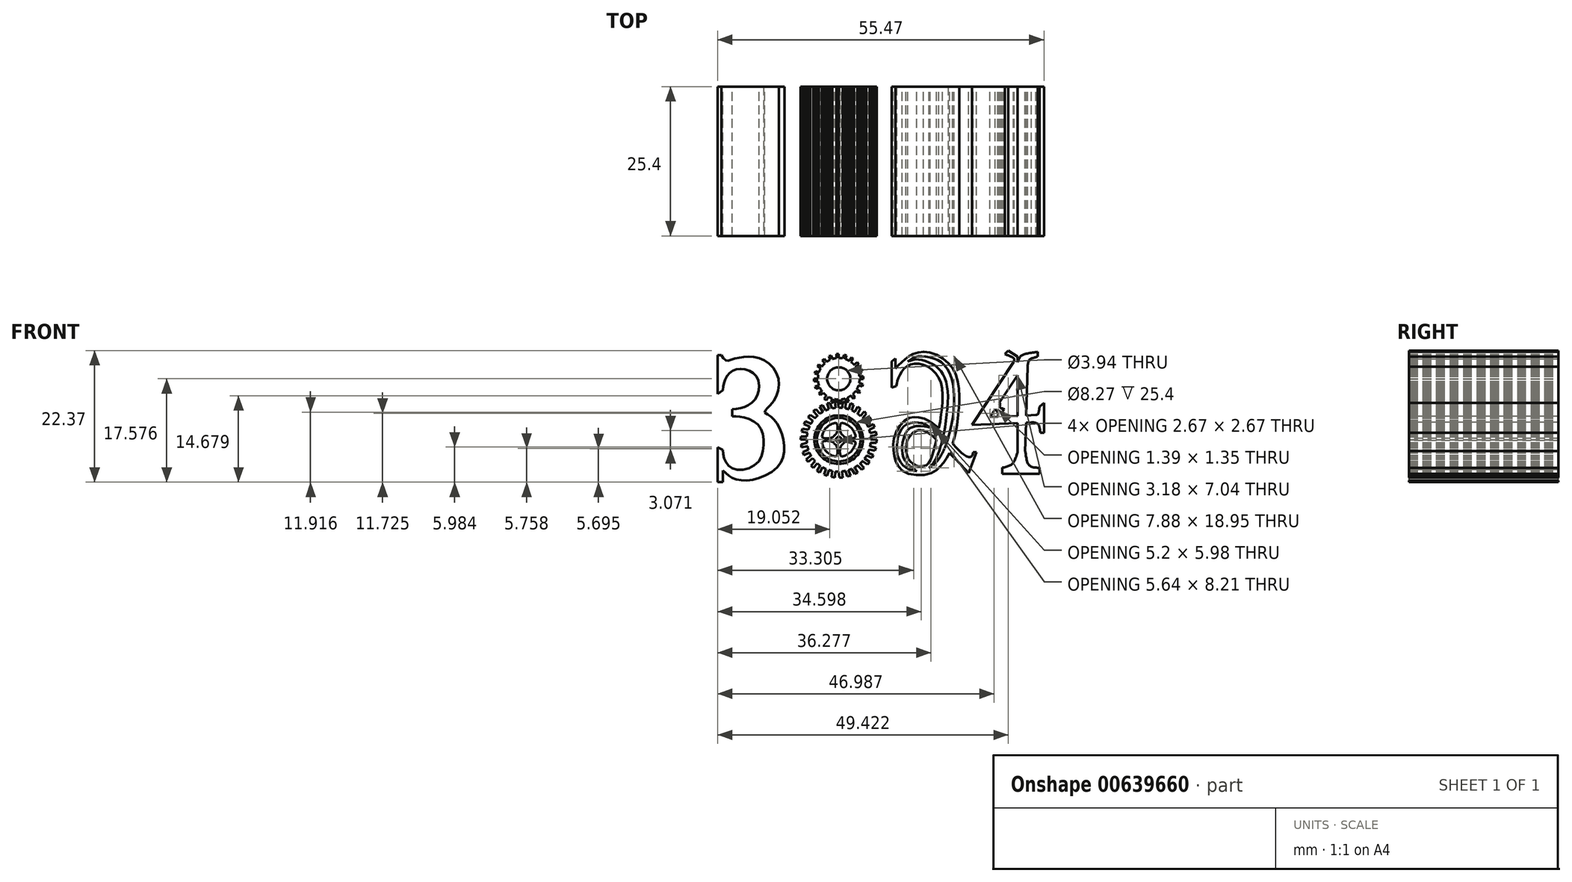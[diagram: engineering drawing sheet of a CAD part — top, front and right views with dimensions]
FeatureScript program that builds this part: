
annotation { "Feature Type Name" : "Feature", "Feature Type Description" : "" }
export const myFeature = defineFeature(function(context is Context, id is Id, definition is map)
    precondition{}
    {
        {
            var Q0;
            Q0=qCreatedBy(makeId("Front.planeOp"),FACE);
            var sketch = newSketch(context, id + "F0", { "sketchPlane" : qUnion([Q0])});
            skLineSegment(sketch, "E0", {"start": v(-26.94, -3.78) * mm, "end": v(-26.94, -9.7) * mm});
            skLineSegment(sketch, "E1", {"start": v(-26.94, -9.7) * mm, "end": v(-26.05, -9.7) * mm});
            skLineSegment(sketch, "E2", {"start": v(-26.05, -9.7) * mm, "end": v(-26.05, -7.7) * mm});
            skLineSegment(sketch, "E3", {"start": v(-26.94, -3.78) * mm, "end": v(-26.05, -4.23) * mm});
            skLineSegment(sketch, "E4", {"start": v(-24.48, 2.7) * mm, "end": v(-24.48, 1.47) * mm});
            skLineSegment(sketch, "E5", {"start": v(-26.94, 5.32) * mm, "end": v(-26.94, 11.91) * mm});
            skLineSegment(sketch, "E6", {"start": v(-26.94, 11.91) * mm, "end": v(-26.32, 11.91) * mm});
            skLineSegment(sketch, "E7", {"start": v(-26.94, 5.32) * mm, "end": v(-26.04, 5.95) * mm});
            skFitSpline(sketch, "E8", {"points": [v(-26.05, -4.23) * mm, v(-25.66, -6.1) * mm, v(-23.85, -7.55) * mm, v(-20.23, -6.46) * mm, v(-19.14, -3.06) * mm, v(-20, 0) * mm, v(-22.69, 1.36) * mm, v(-24.48, 1.47) * mm], "startDerivative": vector(1.25, -16.06) * mm, "endDerivative": vector(-14.31, -0.38) * mm});
            skFitSpline(sketch, "E9", {"points": [v(-26.04, 5.95) * mm, v(-25.74, 7.63) * mm, v(-24.48, 9.18) * mm, v(-22.24, 9.47) * mm, v(-20.15, 7.9) * mm, v(-20.32, 4.8) * mm, v(-22.22, 3.17) * mm, v(-24.48, 2.7) * mm], "startDerivative": vector(1.01, 13.85) * mm, "endDerivative": vector(-16.24, -1.9) * mm});
            skFitSpline(sketch, "E10", {"points": [v(-26.05, -7.7) * mm, v(-24.48, -8.97) * mm, v(-21.28, -9.33) * mm, v(-16.43, -6.72) * mm, v(-15.77, -2.52) * mm, v(-17.37, 0.95) * mm, v(-18.96, 2.15) * mm], "startDerivative": vector(10.75, -11.05) * mm, "endDerivative": vector(-12.75, 7.25) * mm});
            skFitSpline(sketch, "E11", {"points": [v(-18.96, 2.15) * mm, v(-18.67, 2.7) * mm, v(-17.08, 4.65) * mm, v(-16.79, 8.49) * mm, v(-19.36, 11.17) * mm, v(-22.4, 11.6) * mm, v(-24.48, 11.17) * mm, v(-25.48, 10.95) * mm, v(-26.32, 11.91) * mm], "startDerivative": vector(2.7, 7.37) * mm, "endDerivative": vector(-8.1, 13.21) * mm});
            skCircle(sketch, "E12", {"center": v(-6.35, 7.88) * mm, "radius": 1.97 * mm});
            skPoint(sketch, "E12.first.point", {"position": v(-7.49, 9.48) * mm});
            skPoint(sketch, "E12.second.point", {"position": v(-5.26, 6.24) * mm});
            skPoint(sketch, "E12.third.point", {"position": v(-4.53, 7.14) * mm});
            skArc(sketch, "E13", {"start": v(-8.75, 10.48) * mm, "mid": v(-9, 10.24) * mm, "end": v(-9.21, 9.96) * mm});
            skArc(sketch, "E14", {"start": v(-8.02, 2.7) * mm, "mid": v(-8.3, 2.61) * mm, "end": v(-8.57, 2.5) * mm});
            skCircle(sketch, "E15", {"center": v(-6.35, -2.47) * mm, "radius": 3.7 * mm});
            skArc(sketch, "E16", {"start": v(-6.82, 0.4) * mm, "mid": v(-8.41, -0.41) * mm, "end": v(-9.22, -2) * mm});
            skArc(sketch, "E17", {"start": v(-7.26, -2.94) * mm, "mid": v(-7.07, -3.2) * mm, "end": v(-6.82, -3.37) * mm});
            skCircle(sketch, "E18", {"center": v(-6.35, -2.47) * mm, "radius": 0.47 * mm});
            skFitSpline(sketch, "E19", {"points": [v(-5.88, -1.57) * mm, v(-6.1, -1) * mm, v(-6.1, 0) * mm, v(-5.88, 0.4) * mm], "startDerivative": vector(-0.8, 1.58) * mm, "endDerivative": vector(0.94, 1.2) * mm});
            skFitSpline(sketch, "E20.MirrorCS", {"points": [v(-6.82, -1.57) * mm, v(-6.6, -1) * mm, v(-6.6, 0) * mm, v(-6.82, 0.4) * mm], "startDerivative": vector(0.8, 1.58) * mm, "endDerivative": vector(-0.94, 1.2) * mm});
            skFitSpline(sketch, "E21.MirrorCS", {"points": [v(-6.82, -3.37) * mm, v(-6.6, -3.95) * mm, v(-6.6, -4.94) * mm, v(-6.82, -5.34) * mm], "startDerivative": vector(0.8, -1.58) * mm, "endDerivative": vector(-0.94, -1.2) * mm});
            skFitSpline(sketch, "E22.MirrorCS", {"points": [v(-5.88, -3.37) * mm, v(-6.1, -3.95) * mm, v(-6.1, -4.94) * mm, v(-5.88, -5.34) * mm], "startDerivative": vector(-0.8, -1.58) * mm, "endDerivative": vector(0.94, -1.2) * mm});
            skFitSpline(sketch, "E23.MirrorCS", {"points": [v(-7.26, -2) * mm, v(-7.83, -2.22) * mm, v(-8.82, -2.22) * mm, v(-9.22, -2) * mm], "startDerivative": vector(-1.58, -0.8) * mm, "endDerivative": vector(-1.2, 0.94) * mm});
            skFitSpline(sketch, "E24.MirrorCS", {"points": [v(-7.26, -2.94) * mm, v(-7.83, -2.72) * mm, v(-8.82, -2.72) * mm, v(-9.22, -2.94) * mm], "startDerivative": vector(-1.58, 0.8) * mm, "endDerivative": vector(-1.2, -0.94) * mm});
            skFitSpline(sketch, "E25.MirrorCS", {"points": [v(-5.45, -2.94) * mm, v(-4.87, -2.72) * mm, v(-3.88, -2.72) * mm, v(-3.48, -2.94) * mm], "startDerivative": vector(1.58, 0.8) * mm, "endDerivative": vector(1.2, -0.94) * mm});
            skFitSpline(sketch, "E26.MirrorCS", {"points": [v(-5.45, -2) * mm, v(-4.87, -2.22) * mm, v(-3.88, -2.22) * mm, v(-3.48, -2) * mm], "startDerivative": vector(1.58, -0.8) * mm, "endDerivative": vector(1.2, 0.94) * mm});
            skArc(sketch, "E27.trimOffspring", {"start": v(-9.22, -2.94) * mm, "mid": v(-8.41, -4.53) * mm, "end": v(-6.82, -5.34) * mm});
            skArc(sketch, "E28.trimOffspring", {"start": v(-5.88, -5.34) * mm, "mid": v(-4.3, -4.53) * mm, "end": v(-3.48, -2.94) * mm});
            skArc(sketch, "E29.trimOffspring", {"start": v(-3.48, -2) * mm, "mid": v(-4.3, -0.41) * mm, "end": v(-5.88, 0.4) * mm});
            skLineSegment(sketch, "E30", {"start": v(2.67, 6.4) * mm, "end": v(2.67, 10.85) * mm});
            skLineSegment(sketch, "E31", {"start": v(2.67, 10.85) * mm, "end": v(3.29, 11.36) * mm});
            skLineSegment(sketch, "E32", {"start": v(3.29, 11.36) * mm, "end": v(3.29, 9.63) * mm});
            skLineSegment(sketch, "E33", {"start": v(2.67, 6.4) * mm, "end": v(3.44, 6.66) * mm});
            skLineSegment(sketch, "E34", {"start": v(16.48, -4.58) * mm, "end": v(17.06, -4.58) * mm});
            skLineSegment(sketch, "E35", {"start": v(17.06, -4.58) * mm, "end": v(15.76, -8.18) * mm});
            skFitSpline(sketch, "E36", {"points": [v(16.48, -4.58) * mm, v(16.22, -5.34) * mm, v(14.95, -5.06) * mm, v(11.76, -1.64) * mm, v(9.18, 0.63) * mm], "startDerivative": vector(-0.7, -6.32) * mm, "endDerivative": vector(-8.2, 6.33) * mm});
            skFitSpline(sketch, "E37", {"points": [v(9.18, 0.63) * mm, v(6.97, 1.33) * mm, v(5.27, 1.07) * mm, v(3.29, -1.43) * mm, v(2.94, -4.08) * mm, v(3.44, -6.35) * mm, v(5.1, -8.14) * mm, v(9.18, -8.24) * mm, v(11.02, -6.93) * mm, v(12.2, -5.25) * mm, v(13.2, -2.53) * mm, v(13.92, 1.23) * mm, v(14.06, 6.11) * mm, v(12.66, 10.14) * mm, v(8.84, 12.43) * mm, v(6.13, 12.01) * mm, v(4.54, 10.91) * mm, v(3.29, 9.63) * mm], "startDerivative": vector(-48.3, 32.45) * mm, "endDerivative": vector(-26.18, -28.2) * mm});
            skFitSpline(sketch, "E38", {"points": [v(3.44, 6.66) * mm, v(3.7, 7.84) * mm, v(4.8, 9.63) * mm, v(7.16, 10.46) * mm, v(10.5, 8.33) * mm, v(11.14, 2.44) * mm, v(9.72, -4.58) * mm, v(8.52, -6.8) * mm, v(6.55, -6.77) * mm, v(5.27, -5.22) * mm, v(5.27, -2.7) * mm, v(6.84, -0.95) * mm, v(8.07, -0.95) * mm], "startDerivative": vector(3.19, 20.16) * mm, "endDerivative": vector(21.42, -4.51) * mm});
            skFitSpline(sketch, "E39", {"points": [v(15.76, -8.18) * mm, v(14.53, -6.87) * mm, v(11.66, -3.9) * mm, v(9.18, -1.53) * mm, v(8.07, -0.95) * mm], "startDerivative": vector(-5.12, 5.56) * mm, "endDerivative": vector(-5.94, 2.42) * mm});
            skLineSegment(sketch, "E40", {"start": v(25.76, 9.93) * mm, "end": v(25.52, 1.64) * mm});
            skLineSegment(sketch, "E41", {"start": v(24.07, 8.5) * mm, "end": v(24.07, 1.57) * mm});
            skLineSegment(sketch, "E42", {"start": v(16.29, 0) * mm, "end": v(24.07, 0.36) * mm});
            skLineSegment(sketch, "E43", {"start": v(16.29, 0) * mm, "end": v(23.35, 10.7) * mm});
            skLineSegment(sketch, "E44", {"start": v(19.35, 1.35) * mm, "end": v(20.24, 2.7) * mm});
            skLineSegment(sketch, "E45", {"start": v(19.35, 1.35) * mm, "end": v(20.7, 1.42) * mm});
            skLineSegment(sketch, "E46", {"start": v(21.44, -8.3) * mm, "end": v(27.78, -8.3) * mm});
            skFitSpline(sketch, "E47", {"points": [v(25.34, -4.4) * mm, v(25.48, -5.26) * mm, v(25.86, -6.62) * mm, v(26.6, -7.15) * mm, v(27.78, -7.28) * mm], "startDerivative": vector(0.52, -3.36) * mm, "endDerivative": vector(3.73, -0.32) * mm});
            skLineSegment(sketch, "E48", {"start": v(27.78, -7.28) * mm, "end": v(27.78, -8.3) * mm});
            skFitSpline(sketch, "E49.MirrorCS", {"points": [v(24.07, -4.5) * mm, v(23.78, -5.48) * mm, v(23.2, -6.52) * mm, v(22.42, -7) * mm, v(21.44, -7.22) * mm], "startDerivative": vector(-0.76, -3.31) * mm, "endDerivative": vector(-3.74, -0.05) * mm});
            skLineSegment(sketch, "E50", {"start": v(21.44, -7.22) * mm, "end": v(21.44, -8.3) * mm});
            skLineSegment(sketch, "E51", {"start": v(27.92, -1.3) * mm, "end": v(28.53, -1.3) * mm});
            skLineSegment(sketch, "E52", {"start": v(28.53, -1.3) * mm, "end": v(28.53, 3.76) * mm});
            skLineSegment(sketch, "E53", {"start": v(28.53, 3.76) * mm, "end": v(27.8, 3.13) * mm});
            skFitSpline(sketch, "E54", {"points": [v(27.19, 1.72) * mm, v(27.46, 1.81) * mm, v(27.58, 1.97) * mm, v(27.8, 3.13) * mm], "startDerivative": vector(1.17, 0.32) * mm, "endDerivative": vector(0.4, 2.73) * mm});
            skFitSpline(sketch, "E55", {"points": [v(26.38, 0.47) * mm, v(27.08, 0.4) * mm, v(27.63, 0) * mm, v(27.92, -1.3) * mm], "startDerivative": vector(2.42, -0.09) * mm, "endDerivative": vector(0.38, -3.64) * mm});
            skLineSegment(sketch, "E56.trimOffspring", {"start": v(24.07, 0.36) * mm, "end": v(24.07, -4.5) * mm});
            skLineSegment(sketch, "E57.trimOffspring", {"start": v(25.52, 1.64) * mm, "end": v(27.19, 1.72) * mm});
            skLineSegment(sketch, "E58.trimOffspring", {"start": v(25.48, 0.43) * mm, "end": v(25.34, -4.4) * mm});
            skLineSegment(sketch, "E59.trimOffspring", {"start": v(25.48, 0.43) * mm, "end": v(26.38, 0.47) * mm});
            skLineSegment(sketch, "E60", {"start": v(24.07, 10.7) * mm, "end": v(24.07, 11.67) * mm});
            skLineSegment(sketch, "E61", {"start": v(24.07, 11.67) * mm, "end": v(22.47, 12.67) * mm});
            skLineSegment(sketch, "E62", {"start": v(22.47, 12.67) * mm, "end": v(21.91, 12.1) * mm});
            skFitSpline(sketch, "E63", {"points": [v(21.91, 12.1) * mm, v(22.88, 11.68) * mm, v(23.32, 11.44) * mm, v(23.46, 11.24) * mm, v(23.35, 10.7) * mm], "startDerivative": vector(2, -1.3) * mm, "endDerivative": vector(-1.38, -1.95) * mm});
            skPoint(sketch, "E64.0.internal.snap0", {"position": v(24.07, 10.8) * mm});
            skFitSpline(sketch, "E64", {"points": [v(24.07, 10.7) * mm, v(24.48, 11.62) * mm, v(25.36, 12.1) * mm, v(27.5, 12.45) * mm], "startDerivative": vector(1.5, 3.56) * mm, "endDerivative": vector(4.9, 0.67) * mm});
            skFitSpline(sketch, "E65", {"points": [v(25.76, 9.93) * mm, v(25.87, 10.7) * mm, v(26.24, 11.24) * mm, v(27.5, 11.66) * mm], "startDerivative": vector(0.1, 2.05) * mm, "endDerivative": vector(2.59, 0.85) * mm});
            skLineSegment(sketch, "E66", {"start": v(27.5, 12.45) * mm, "end": v(27.5, 11.66) * mm});
            skLineSegment(sketch, "E67.bottom", {"start": v(-6.76, 11.4) * mm, "end": v(-6.34, 11.4) * mm});
            skLineSegment(sketch, "E67.top", {"start": v(-6.76, 12.07) * mm, "end": v(-6.34, 12.07) * mm});
            skLineSegment(sketch, "E67.left", {"start": v(-6.76, 11.4) * mm, "end": v(-6.76, 12.07) * mm});
            skLineSegment(sketch, "E67.right", {"start": v(-6.34, 11.4) * mm, "end": v(-6.34, 12.07) * mm});
            skLineSegment(sketch, "E68.1.0", {"start": v(-7.82, 11.1) * mm, "end": v(-8.03, 11.74) * mm});
            skLineSegment(sketch, "E68.1.1", {"start": v(-8.03, 11.74) * mm, "end": v(-7.64, 11.86) * mm});
            skLineSegment(sketch, "E68.1.2", {"start": v(-7.43, 11.22) * mm, "end": v(-7.64, 11.86) * mm});
            skLineSegment(sketch, "E68.2.0", {"start": v(-8.75, 10.48) * mm, "end": v(-9.14, 11.03) * mm});
            skLineSegment(sketch, "E68.2.1", {"start": v(-9.14, 11.03) * mm, "end": v(-8.8, 11.27) * mm});
            skLineSegment(sketch, "E68.2.2", {"start": v(-8.41, 10.73) * mm, "end": v(-8.8, 11.27) * mm});
            skLineSegment(sketch, "E68.3.0", {"start": v(-9.44, 9.62) * mm, "end": v(-9.98, 10.01) * mm});
            skLineSegment(sketch, "E68.3.1", {"start": v(-9.98, 10.01) * mm, "end": v(-9.74, 10.35) * mm});
            skLineSegment(sketch, "E68.3.2", {"start": v(-9.2, 9.95) * mm, "end": v(-9.74, 10.35) * mm});
            skLineSegment(sketch, "E68.4.0", {"start": v(-9.82, 8.58) * mm, "end": v(-10.46, 8.79) * mm});
            skLineSegment(sketch, "E68.4.1", {"start": v(-10.46, 8.79) * mm, "end": v(-10.34, 9.18) * mm});
            skLineSegment(sketch, "E68.4.2", {"start": v(-9.7, 8.97) * mm, "end": v(-10.34, 9.18) * mm});
            skLineSegment(sketch, "E68.5.0", {"start": v(-9.87, 7.47) * mm, "end": v(-10.54, 7.47) * mm});
            skLineSegment(sketch, "E68.5.1", {"start": v(-10.54, 7.47) * mm, "end": v(-10.54, 7.88) * mm});
            skLineSegment(sketch, "E68.5.2", {"start": v(-9.87, 7.88) * mm, "end": v(-10.54, 7.88) * mm});
            skLineSegment(sketch, "E68.6.0", {"start": v(-9.57, 6.4) * mm, "end": v(-10.21, 6.2) * mm});
            skLineSegment(sketch, "E68.6.1", {"start": v(-10.21, 6.2) * mm, "end": v(-10.34, 6.59) * mm});
            skLineSegment(sketch, "E68.6.2", {"start": v(-9.7, 6.8) * mm, "end": v(-10.34, 6.59) * mm});
            skLineSegment(sketch, "E68.7.0", {"start": v(-8.96, 5.48) * mm, "end": v(-9.5, 5.09) * mm});
            skLineSegment(sketch, "E68.7.1", {"start": v(-9.5, 5.09) * mm, "end": v(-9.75, 5.42) * mm});
            skLineSegment(sketch, "E68.7.2", {"start": v(-9.2, 5.82) * mm, "end": v(-9.75, 5.42) * mm});
            skLineSegment(sketch, "E68.8.0", {"start": v(-8.1, 4.8) * mm, "end": v(-8.49, 4.25) * mm});
            skLineSegment(sketch, "E68.8.1", {"start": v(-8.49, 4.25) * mm, "end": v(-8.82, 4.5) * mm});
            skLineSegment(sketch, "E68.8.2", {"start": v(-8.43, 5.04) * mm, "end": v(-8.82, 4.5) * mm});
            skLineSegment(sketch, "E68.9.0", {"start": v(-7.05, 4.4) * mm, "end": v(-7.26, 3.77) * mm});
            skLineSegment(sketch, "E68.9.1", {"start": v(-7.26, 3.77) * mm, "end": v(-7.66, 3.9) * mm});
            skLineSegment(sketch, "E68.9.2", {"start": v(-7.45, 4.53) * mm, "end": v(-7.66, 3.9) * mm});
            skLineSegment(sketch, "E68.10.0", {"start": v(-5.95, 4.36) * mm, "end": v(-5.95, 3.69) * mm});
            skLineSegment(sketch, "E68.10.1", {"start": v(-5.95, 3.69) * mm, "end": v(-6.36, 3.69) * mm});
            skLineSegment(sketch, "E68.10.2", {"start": v(-6.36, 4.36) * mm, "end": v(-6.36, 3.69) * mm});
            skLineSegment(sketch, "E68.11.0", {"start": v(-4.88, 4.66) * mm, "end": v(-4.67, 4.02) * mm});
            skLineSegment(sketch, "E68.11.1", {"start": v(-4.67, 4.02) * mm, "end": v(-5.07, 3.89) * mm});
            skLineSegment(sketch, "E68.11.2", {"start": v(-5.27, 4.53) * mm, "end": v(-5.07, 3.89) * mm});
            skLineSegment(sketch, "E68.12.0", {"start": v(-3.96, 5.27) * mm, "end": v(-3.56, 4.72) * mm});
            skLineSegment(sketch, "E68.12.1", {"start": v(-3.56, 4.72) * mm, "end": v(-3.9, 4.48) * mm});
            skLineSegment(sketch, "E68.12.2", {"start": v(-4.3, 5.03) * mm, "end": v(-3.9, 4.48) * mm});
            skLineSegment(sketch, "E68.13.0", {"start": v(-3.27, 6.14) * mm, "end": v(-2.72, 5.74) * mm});
            skLineSegment(sketch, "E68.13.1", {"start": v(-2.72, 5.74) * mm, "end": v(-2.97, 5.4) * mm});
            skLineSegment(sketch, "E68.13.2", {"start": v(-3.51, 5.8) * mm, "end": v(-2.97, 5.4) * mm});
            skLineSegment(sketch, "E68.14.0", {"start": v(-2.88, 7.17) * mm, "end": v(-2.24, 6.97) * mm});
            skLineSegment(sketch, "E68.14.1", {"start": v(-2.24, 6.97) * mm, "end": v(-2.37, 6.57) * mm});
            skLineSegment(sketch, "E68.14.2", {"start": v(-3.01, 6.78) * mm, "end": v(-2.37, 6.57) * mm});
            skLineSegment(sketch, "E68.15.0", {"start": v(-2.84, 8.28) * mm, "end": v(-2.16, 8.28) * mm});
            skLineSegment(sketch, "E68.15.1", {"start": v(-2.16, 8.28) * mm, "end": v(-2.16, 7.87) * mm});
            skLineSegment(sketch, "E68.15.2", {"start": v(-2.84, 7.87) * mm, "end": v(-2.16, 7.87) * mm});
            skLineSegment(sketch, "E68.16.0", {"start": v(-3.13, 9.35) * mm, "end": v(-2.5, 9.56) * mm});
            skLineSegment(sketch, "E68.16.1", {"start": v(-2.5, 9.56) * mm, "end": v(-2.37, 9.16) * mm});
            skLineSegment(sketch, "E68.16.2", {"start": v(-3, 8.95) * mm, "end": v(-2.37, 9.16) * mm});
            skLineSegment(sketch, "E68.17.0", {"start": v(-3.75, 10.27) * mm, "end": v(-3.2, 10.67) * mm});
            skLineSegment(sketch, "E68.17.1", {"start": v(-3.2, 10.67) * mm, "end": v(-2.96, 10.33) * mm});
            skLineSegment(sketch, "E68.17.2", {"start": v(-3.5, 9.94) * mm, "end": v(-2.96, 10.33) * mm});
            skLineSegment(sketch, "E68.18.0", {"start": v(-4.61, 10.96) * mm, "end": v(-4.22, 11.5) * mm});
            skLineSegment(sketch, "E68.18.1", {"start": v(-4.22, 11.5) * mm, "end": v(-3.88, 11.26) * mm});
            skLineSegment(sketch, "E68.18.2", {"start": v(-4.28, 10.72) * mm, "end": v(-3.88, 11.26) * mm});
            skLineSegment(sketch, "E68.19.0", {"start": v(-5.65, 11.35) * mm, "end": v(-5.44, 11.99) * mm});
            skLineSegment(sketch, "E68.19.1", {"start": v(-5.44, 11.99) * mm, "end": v(-5.05, 11.86) * mm});
            skLineSegment(sketch, "E68.19.2", {"start": v(-5.26, 11.22) * mm, "end": v(-5.05, 11.86) * mm});
            skArc(sketch, "E69.trimOffspring", {"start": v(-7.82, 11.1) * mm, "mid": v(-8.13, 10.94) * mm, "end": v(-8.43, 10.75) * mm});
            skArc(sketch, "E70.trimOffspring", {"start": v(-6.76, 11.4) * mm, "mid": v(-7.1, 11.34) * mm, "end": v(-7.44, 11.25) * mm});
            skArc(sketch, "E71.trimOffspring", {"start": v(-5.65, 11.35) * mm, "mid": v(-6, 11.4) * mm, "end": v(-6.34, 11.42) * mm});
            skArc(sketch, "E72.trimOffspring", {"start": v(-4.61, 10.96) * mm, "mid": v(-4.92, 11.12) * mm, "end": v(-5.25, 11.24) * mm});
            skArc(sketch, "E73.trimOffspring", {"start": v(-3.75, 10.27) * mm, "mid": v(-4, 10.52) * mm, "end": v(-4.26, 10.74) * mm});
            skArc(sketch, "E74.trimOffspring", {"start": v(-3.13, 9.35) * mm, "mid": v(-3.3, 9.66) * mm, "end": v(-3.48, 9.95) * mm});
            skArc(sketch, "E75.trimOffspring", {"start": v(-2.84, 8.28) * mm, "mid": v(-2.9, 8.63) * mm, "end": v(-2.98, 8.96) * mm});
            skArc(sketch, "E76.trimOffspring", {"start": v(-2.88, 7.17) * mm, "mid": v(-2.83, 7.52) * mm, "end": v(-2.81, 7.87) * mm});
            skArc(sketch, "E77.trimOffspring", {"start": v(-3.27, 6.14) * mm, "mid": v(-3.11, 6.45) * mm, "end": v(-2.99, 6.77) * mm});
            skArc(sketch, "E78.trimOffspring", {"start": v(-3.96, 5.27) * mm, "mid": v(-3.71, 5.52) * mm, "end": v(-3.5, 5.79) * mm});
            skArc(sketch, "E79.trimOffspring", {"start": v(-4.88, 4.66) * mm, "mid": v(-4.57, 4.82) * mm, "end": v(-4.28, 5) * mm});
            skArc(sketch, "E80.trimOffspring", {"start": v(-5.95, 4.36) * mm, "mid": v(-5.6, 4.42) * mm, "end": v(-5.27, 4.5) * mm});
            skArc(sketch, "E81.trimOffspring", {"start": v(-7.05, 4.4) * mm, "mid": v(-6.7, 4.35) * mm, "end": v(-6.36, 4.34) * mm});
            skArc(sketch, "E82.trimOffspring", {"start": v(-8.1, 4.8) * mm, "mid": v(-7.78, 4.64) * mm, "end": v(-7.45, 4.51) * mm});
            skArc(sketch, "E83.trimOffspring", {"start": v(-8.96, 5.48) * mm, "mid": v(-8.71, 5.24) * mm, "end": v(-8.44, 5.02) * mm});
            skArc(sketch, "E84.trimOffspring", {"start": v(-9.57, 6.4) * mm, "mid": v(-9.41, 6.1) * mm, "end": v(-9.22, 5.8) * mm});
            skArc(sketch, "E85.trimOffspring", {"start": v(-9.87, 7.47) * mm, "mid": v(-9.81, 7.13) * mm, "end": v(-9.72, 6.79) * mm});
            skArc(sketch, "E86.trimOffspring", {"start": v(-9.82, 8.58) * mm, "mid": v(-9.88, 8.23) * mm, "end": v(-9.9, 7.88) * mm});
            skArc(sketch, "E87.trimOffspring", {"start": v(-9.44, 9.62) * mm, "mid": v(-9.6, 9.3) * mm, "end": v(-9.72, 8.98) * mm});
            skPoint(sketch, "E88.startSnap0", {"position": v(-6.36, 4.02) * mm});
            skLineSegment(sketch, "E89", {"start": v(-6.48, 3.97) * mm, "end": v(-7.02, 3.97) * mm});
            skLineSegment(sketch, "E90", {"start": v(-7.02, 3.97) * mm, "end": v(-6.9, 2.94) * mm});
            skLineSegment(sketch, "E91", {"start": v(-6.48, 3.97) * mm, "end": v(-6.36, 2.97) * mm});
            skLineSegment(sketch, "E92.1.0", {"start": v(-7.81, 3.8) * mm, "end": v(-8.35, 3.7) * mm});
            skLineSegment(sketch, "E92.1.1", {"start": v(-7.81, 3.8) * mm, "end": v(-7.5, 2.85) * mm});
            skLineSegment(sketch, "E92.1.2", {"start": v(-8.35, 3.7) * mm, "end": v(-8.02, 2.7) * mm});
            skLineSegment(sketch, "E92.2.0", {"start": v(-9.09, 3.36) * mm, "end": v(-9.59, 3.14) * mm});
            skLineSegment(sketch, "E92.2.1", {"start": v(-9.09, 3.36) * mm, "end": v(-8.57, 2.5) * mm});
            skLineSegment(sketch, "E92.2.2", {"start": v(-9.59, 3.14) * mm, "end": v(-9.06, 2.25) * mm});
            skLineSegment(sketch, "E92.3.0", {"start": v(-10.24, 2.67) * mm, "end": v(-10.68, 2.35) * mm});
            skLineSegment(sketch, "E92.3.1", {"start": v(-10.24, 2.67) * mm, "end": v(-9.56, 1.93) * mm});
            skLineSegment(sketch, "E92.3.2", {"start": v(-10.68, 2.35) * mm, "end": v(-9.98, 1.58) * mm});
            skLineSegment(sketch, "E92.4.0", {"start": v(-11.22, 1.75) * mm, "end": v(-11.59, 1.34) * mm});
            skLineSegment(sketch, "E92.4.1", {"start": v(-11.22, 1.75) * mm, "end": v(-10.4, 1.16) * mm});
            skLineSegment(sketch, "E92.4.2", {"start": v(-11.59, 1.34) * mm, "end": v(-10.74, 0.74) * mm});
            skLineSegment(sketch, "E92.5.0", {"start": v(-12, 0.64) * mm, "end": v(-12.27, 0.17) * mm});
            skLineSegment(sketch, "E92.5.1", {"start": v(-12, 0.64) * mm, "end": v(-11.07, 0.24) * mm});
            skLineSegment(sketch, "E92.5.2", {"start": v(-12.27, 0.17) * mm, "end": v(-11.32, -0.24) * mm});
            skLineSegment(sketch, "E92.6.0", {"start": v(-12.52, -0.6) * mm, "end": v(-12.69, -1.12) * mm});
            skLineSegment(sketch, "E92.6.1", {"start": v(-12.52, -0.6) * mm, "end": v(-11.53, -0.8) * mm});
            skLineSegment(sketch, "E92.6.2", {"start": v(-12.69, -1.12) * mm, "end": v(-11.67, -1.32) * mm});
            skLineSegment(sketch, "E92.7.0", {"start": v(-12.77, -1.92) * mm, "end": v(-12.83, -2.46) * mm});
            skLineSegment(sketch, "E92.7.1", {"start": v(-12.77, -1.92) * mm, "end": v(-11.76, -1.9) * mm});
            skLineSegment(sketch, "E92.7.2", {"start": v(-12.83, -2.46) * mm, "end": v(-11.8, -2.45) * mm});
            skLineSegment(sketch, "E92.8.0", {"start": v(-12.75, -3.27) * mm, "end": v(-12.69, -3.81) * mm});
            skLineSegment(sketch, "E92.8.1", {"start": v(-12.75, -3.27) * mm, "end": v(-11.76, -3.05) * mm});
            skLineSegment(sketch, "E92.8.2", {"start": v(-12.69, -3.81) * mm, "end": v(-11.68, -3.58) * mm});
            skLineSegment(sketch, "E92.9.0", {"start": v(-12.44, -4.58) * mm, "end": v(-12.27, -5.1) * mm});
            skLineSegment(sketch, "E92.9.1", {"start": v(-12.44, -4.58) * mm, "end": v(-11.52, -4.16) * mm});
            skLineSegment(sketch, "E92.9.2", {"start": v(-12.27, -5.1) * mm, "end": v(-11.33, -4.67) * mm});
            skLineSegment(sketch, "E92.10.0", {"start": v(-11.87, -5.8) * mm, "end": v(-11.6, -6.27) * mm});
            skLineSegment(sketch, "E92.10.1", {"start": v(-11.87, -5.8) * mm, "end": v(-11.06, -5.2) * mm});
            skLineSegment(sketch, "E92.10.2", {"start": v(-11.6, -6.27) * mm, "end": v(-10.76, -5.65) * mm});
            skLineSegment(sketch, "E92.11.0", {"start": v(-11.06, -6.87) * mm, "end": v(-10.7, -7.28) * mm});
            skLineSegment(sketch, "E92.11.1", {"start": v(-11.06, -6.87) * mm, "end": v(-10.4, -6.12) * mm});
            skLineSegment(sketch, "E92.11.2", {"start": v(-10.7, -7.28) * mm, "end": v(-10, -6.5) * mm});
            skLineSegment(sketch, "E92.12.0", {"start": v(-10.04, -7.76) * mm, "end": v(-9.6, -8.08) * mm});
            skLineSegment(sketch, "E92.12.1", {"start": v(-10.04, -7.76) * mm, "end": v(-9.54, -6.88) * mm});
            skLineSegment(sketch, "E92.12.2", {"start": v(-9.6, -8.08) * mm, "end": v(-9.09, -7.17) * mm});
            skLineSegment(sketch, "E92.13.0", {"start": v(-8.86, -8.4) * mm, "end": v(-8.36, -8.63) * mm});
            skLineSegment(sketch, "E92.13.1", {"start": v(-8.86, -8.4) * mm, "end": v(-8.56, -7.44) * mm});
            skLineSegment(sketch, "E92.13.2", {"start": v(-8.36, -8.63) * mm, "end": v(-8.05, -7.64) * mm});
            skLineSegment(sketch, "E92.14.0", {"start": v(-7.57, -8.8) * mm, "end": v(-7.03, -8.91) * mm});
            skLineSegment(sketch, "E92.14.1", {"start": v(-7.57, -8.8) * mm, "end": v(-7.48, -7.8) * mm});
            skLineSegment(sketch, "E92.14.2", {"start": v(-7.03, -8.91) * mm, "end": v(-6.94, -7.88) * mm});
            skLineSegment(sketch, "E92.15.0", {"start": v(-6.23, -8.91) * mm, "end": v(-5.68, -8.91) * mm});
            skLineSegment(sketch, "E92.15.1", {"start": v(-6.23, -8.91) * mm, "end": v(-6.34, -7.91) * mm});
            skLineSegment(sketch, "E92.15.2", {"start": v(-5.68, -8.91) * mm, "end": v(-5.8, -7.88) * mm});
            skLineSegment(sketch, "E92.16.0", {"start": v(-4.9, -8.75) * mm, "end": v(-4.36, -8.63) * mm});
            skLineSegment(sketch, "E92.16.1", {"start": v(-4.9, -8.75) * mm, "end": v(-5.21, -7.79) * mm});
            skLineSegment(sketch, "E92.16.2", {"start": v(-4.36, -8.63) * mm, "end": v(-4.69, -7.65) * mm});
            skLineSegment(sketch, "E92.17.0", {"start": v(-3.62, -8.3) * mm, "end": v(-3.12, -8.08) * mm});
            skLineSegment(sketch, "E92.17.1", {"start": v(-3.62, -8.3) * mm, "end": v(-4.13, -7.44) * mm});
            skLineSegment(sketch, "E92.17.2", {"start": v(-3.12, -8.08) * mm, "end": v(-3.65, -7.19) * mm});
            skLineSegment(sketch, "E92.18.0", {"start": v(-2.46, -7.6) * mm, "end": v(-2.02, -7.29) * mm});
            skLineSegment(sketch, "E92.18.1", {"start": v(-2.46, -7.6) * mm, "end": v(-3.15, -6.87) * mm});
            skLineSegment(sketch, "E92.18.2", {"start": v(-2.02, -7.29) * mm, "end": v(-2.73, -6.52) * mm});
            skLineSegment(sketch, "E92.19.0", {"start": v(-1.48, -6.69) * mm, "end": v(-1.12, -6.28) * mm});
            skLineSegment(sketch, "E92.19.1", {"start": v(-1.48, -6.69) * mm, "end": v(-2.3, -6.1) * mm});
            skLineSegment(sketch, "E92.19.2", {"start": v(-1.12, -6.28) * mm, "end": v(-1.96, -5.68) * mm});
            skLineSegment(sketch, "E92.20.0", {"start": v(-0.71, -5.58) * mm, "end": v(-0.44, -5.1) * mm});
            skLineSegment(sketch, "E92.20.1", {"start": v(-0.71, -5.58) * mm, "end": v(-1.64, -5.18) * mm});
            skLineSegment(sketch, "E92.20.2", {"start": v(-0.44, -5.1) * mm, "end": v(-1.39, -4.7) * mm});
            skLineSegment(sketch, "E92.21.0", {"start": v(-0.19, -4.34) * mm, "end": v(-0.02, -3.82) * mm});
            skLineSegment(sketch, "E92.21.1", {"start": v(-0.19, -4.34) * mm, "end": v(-1.18, -4.14) * mm});
            skLineSegment(sketch, "E92.21.2", {"start": v(-0.02, -3.82) * mm, "end": v(-1.03, -3.62) * mm});
            skLineSegment(sketch, "E92.22.0", {"start": v(0.07, -3.02) * mm, "end": v(0.12, -2.48) * mm});
            skLineSegment(sketch, "E92.22.1", {"start": v(0.07, -3.02) * mm, "end": v(-0.94, -3.03) * mm});
            skLineSegment(sketch, "E92.22.2", {"start": v(0.12, -2.48) * mm, "end": v(-0.91, -2.49) * mm});
            skLineSegment(sketch, "E92.23.0", {"start": v(0.04, -1.67) * mm, "end": v(-0.02, -1.13) * mm});
            skLineSegment(sketch, "E92.23.1", {"start": v(0.04, -1.67) * mm, "end": v(-0.94, -1.9) * mm});
            skLineSegment(sketch, "E92.23.2", {"start": v(-0.02, -1.13) * mm, "end": v(-1.03, -1.36) * mm});
            skLineSegment(sketch, "E92.24.0", {"start": v(-0.26, -0.36) * mm, "end": v(-0.43, 0.16) * mm});
            skLineSegment(sketch, "E92.24.1", {"start": v(-0.26, -0.36) * mm, "end": v(-1.18, -0.78) * mm});
            skLineSegment(sketch, "E92.24.2", {"start": v(-0.43, 0.16) * mm, "end": v(-1.38, -0.27) * mm});
            skLineSegment(sketch, "E92.25.0", {"start": v(-0.84, 0.86) * mm, "end": v(-1.1, 1.33) * mm});
            skLineSegment(sketch, "E92.25.1", {"start": v(-0.84, 0.86) * mm, "end": v(-1.65, 0.26) * mm});
            skLineSegment(sketch, "E92.25.2", {"start": v(-1.1, 1.33) * mm, "end": v(-1.94, 0.71) * mm});
            skLineSegment(sketch, "E92.26.0", {"start": v(-1.65, 1.93) * mm, "end": v(-2.01, 2.34) * mm});
            skLineSegment(sketch, "E92.26.1", {"start": v(-1.65, 1.93) * mm, "end": v(-2.32, 1.18) * mm});
            skLineSegment(sketch, "E92.26.2", {"start": v(-2.01, 2.34) * mm, "end": v(-2.7, 1.56) * mm});
            skLineSegment(sketch, "E92.27.0", {"start": v(-2.67, 2.82) * mm, "end": v(-3.1, 3.14) * mm});
            skLineSegment(sketch, "E92.27.1", {"start": v(-2.67, 2.82) * mm, "end": v(-3.16, 1.94) * mm});
            skLineSegment(sketch, "E92.27.2", {"start": v(-3.1, 3.14) * mm, "end": v(-3.62, 2.23) * mm});
            skLineSegment(sketch, "E92.28.0", {"start": v(-3.85, 3.47) * mm, "end": v(-4.35, 3.69) * mm});
            skLineSegment(sketch, "E92.28.1", {"start": v(-3.85, 3.47) * mm, "end": v(-4.15, 2.5) * mm});
            skLineSegment(sketch, "E92.28.2", {"start": v(-4.35, 3.69) * mm, "end": v(-4.66, 2.7) * mm});
            skLineSegment(sketch, "E92.29.0", {"start": v(-5.14, 3.86) * mm, "end": v(-5.67, 3.97) * mm});
            skLineSegment(sketch, "E92.29.1", {"start": v(-5.14, 3.86) * mm, "end": v(-5.23, 2.85) * mm});
            skLineSegment(sketch, "E92.29.2", {"start": v(-5.67, 3.97) * mm, "end": v(-5.77, 2.94) * mm});
            skArc(sketch, "E93.trimOffspring", {"start": v(-9.06, 2.25) * mm, "mid": v(-9.31, 2.1) * mm, "end": v(-9.56, 1.93) * mm});
            skArc(sketch, "E94.trimOffspring", {"start": v(-9.98, 1.58) * mm, "mid": v(-10.2, 1.38) * mm, "end": v(-10.4, 1.16) * mm});
            skArc(sketch, "E95.trimOffspring", {"start": v(-11.32, -0.24) * mm, "mid": v(-11.43, -0.52) * mm, "end": v(-11.53, -0.8) * mm});
            skArc(sketch, "E96.trimOffspring", {"start": v(-11.8, -2.45) * mm, "mid": v(-11.79, -2.75) * mm, "end": v(-11.76, -3.05) * mm});
            skArc(sketch, "E97.trimOffspring", {"start": v(-10.76, -5.65) * mm, "mid": v(-10.58, -5.9) * mm, "end": v(-10.4, -6.12) * mm});
            skArc(sketch, "E98.trimOffspring", {"start": v(-11.68, -3.58) * mm, "mid": v(-11.6, -3.87) * mm, "end": v(-11.52, -4.16) * mm});
            skArc(sketch, "E99.trimOffspring", {"start": v(-9.09, -7.17) * mm, "mid": v(-8.83, -7.32) * mm, "end": v(-8.56, -7.44) * mm});
            skArc(sketch, "E100.trimOffspring", {"start": v(-6.94, -7.88) * mm, "mid": v(-6.64, -7.9) * mm, "end": v(-6.34, -7.91) * mm});
            skArc(sketch, "E101.trimOffspring", {"start": v(-8.05, -7.64) * mm, "mid": v(-7.77, -7.72) * mm, "end": v(-7.48, -7.8) * mm});
            skArc(sketch, "E102.trimOffspring", {"start": v(-4.69, -7.65) * mm, "mid": v(-4.4, -7.55) * mm, "end": v(-4.13, -7.44) * mm});
            skArc(sketch, "E103.trimOffspring", {"start": v(-2.73, -6.52) * mm, "mid": v(-2.5, -6.32) * mm, "end": v(-2.3, -6.1) * mm});
            skArc(sketch, "E104.trimOffspring", {"start": v(-3.65, -7.19) * mm, "mid": v(-3.4, -7.03) * mm, "end": v(-3.15, -6.87) * mm});
            skArc(sketch, "E105.trimOffspring", {"start": v(-1.96, -5.68) * mm, "mid": v(-1.8, -5.44) * mm, "end": v(-1.64, -5.18) * mm});
            skArc(sketch, "E106.trimOffspring", {"start": v(-1.39, -4.7) * mm, "mid": v(-1.28, -4.42) * mm, "end": v(-1.18, -4.14) * mm});
            skArc(sketch, "E107.trimOffspring", {"start": v(-0.91, -2.49) * mm, "mid": v(-0.92, -2.19) * mm, "end": v(-0.94, -1.9) * mm});
            skArc(sketch, "E108.trimOffspring", {"start": v(-1.38, -0.27) * mm, "mid": v(-1.5, 0) * mm, "end": v(-1.65, 0.26) * mm});
            skArc(sketch, "E109.trimOffspring", {"start": v(-1.94, 0.71) * mm, "mid": v(-2.12, 0.95) * mm, "end": v(-2.32, 1.18) * mm});
            skArc(sketch, "E110.trimOffspring", {"start": v(-2.7, 1.56) * mm, "mid": v(-2.93, 1.76) * mm, "end": v(-3.16, 1.94) * mm});
            skArc(sketch, "E111.trimOffspring", {"start": v(-4.66, 2.7) * mm, "mid": v(-4.94, 2.78) * mm, "end": v(-5.23, 2.85) * mm});
            skArc(sketch, "E112.trimOffspring", {"start": v(-6.9, 2.94) * mm, "mid": v(-7.2, 2.9) * mm, "end": v(-7.5, 2.85) * mm});
            skArc(sketch, "E113.trimOffspring", {"start": v(-5.77, 2.94) * mm, "mid": v(-6.06, 2.96) * mm, "end": v(-6.36, 2.97) * mm});
            skArc(sketch, "E114", {"start": v(20.7, 1.42) * mm, "mid": v(20.67, 2.13) * mm, "end": v(20.24, 2.7) * mm});
            skArc(sketch, "E115", {"start": v(20.7, 3.4) * mm, "mid": v(20.71, 3.4) * mm, "end": v(20.72, 3.4) * mm});
            skLineSegment(sketch, "E116", {"start": v(21.32, 2.74) * mm, "end": v(21.6, 2.92) * mm});
            skLineSegment(sketch, "E117", {"start": v(21.6, 2.92) * mm, "end": v(21.77, 2.65) * mm});
            skLineSegment(sketch, "E118", {"start": v(21.77, 2.65) * mm, "end": v(21.46, 2.45) * mm});
            skLineSegment(sketch, "E119.2.0", {"start": v(21.59, 1.89) * mm, "end": v(21.92, 1.93) * mm});
            skLineSegment(sketch, "E119.2.1", {"start": v(21.92, 1.93) * mm, "end": v(21.96, 1.61) * mm});
            skLineSegment(sketch, "E119.2.2", {"start": v(21.96, 1.61) * mm, "end": v(21.59, 1.57) * mm});
            skLineSegment(sketch, "E119.anchor1", {"start": v(19.53, 1.71) * mm, "end": v(21.32, 2.74) * mm, "construction": true});
            skLineSegment(sketch, "E119.anchor2", {"start": v(19.53, 1.71) * mm, "end": v(21.59, 1.89) * mm, "construction": true});
            skLineSegment(sketch, "E120.2.2", {"start": v(20.9, 3.68) * mm, "end": v(21.17, 3.5) * mm});
            skLineSegment(sketch, "E120.anchor1", {"start": v(19.53, 1.71) * mm, "end": v(21.46, 2.45) * mm, "construction": true});
            skLineSegment(sketch, "E120.anchor2", {"start": v(19.53, 1.71) * mm, "end": v(20.96, 3.2) * mm, "construction": true});
            skLineSegment(sketch, "E121.trimOffspring", {"start": v(20.9, 3.69) * mm, "end": v(24.07, 8.5) * mm});
            skArc(sketch, "E122.trimOffspring", {"start": v(20.96, 3.2) * mm, "mid": v(21.01, 3.15) * mm, "end": v(21.06, 3.1) * mm});
            skArc(sketch, "E123.trimOffspring", {"start": v(21.06, 3.1) * mm, "mid": v(21.2, 2.92) * mm, "end": v(21.32, 2.74) * mm});
            skArc(sketch, "E124.trimOffspring", {"start": v(21.46, 2.45) * mm, "mid": v(21.48, 2.39) * mm, "end": v(21.5, 2.33) * mm});
            skArc(sketch, "E125.trimOffspring", {"start": v(21.5, 2.33) * mm, "mid": v(21.55, 2.1) * mm, "end": v(21.59, 1.89) * mm});
            skArc(sketch, "E126.trimOffspring", {"start": v(21.59, 1.57) * mm, "mid": v(21.58, 1.51) * mm, "end": v(21.58, 1.46) * mm});
            skLineSegment(sketch, "E127.trimOffspring", {"start": v(21.58, 1.46) * mm, "end": v(24.07, 1.57) * mm});
            skFitSpline(sketch, "E128", {"points": [v(5.4, 10.8) * mm, v(6.64, 11.17) * mm, v(8.85, 10.73) * mm, v(10.9, 9.32) * mm, v(12.1, 6.4) * mm, v(11.76, 0) * mm, v(10.3, -5.45) * mm, v(9.01, -7.26) * mm], "startDerivative": vector(12.41, 5.35) * mm, "endDerivative": vector(-11.15, -12.53) * mm});
            skFitSpline(sketch, "E129", {"points": [v(5.4, 10.8) * mm, v(6.64, 11.57) * mm, v(9.17, 11.53) * mm, v(11.98, 9.76) * mm, v(13.27, 3.78) * mm, v(11.34, -4.6) * mm, v(9.01, -7.26) * mm], "startDerivative": vector(10.79, 8.85) * mm, "endDerivative": vector(-16.84, -9.1) * mm});
            skFitSpline(sketch, "E130", {"points": [v(9.18, -0.4) * mm, v(7.57, 0.37) * mm, v(5, 0) * mm, v(3.63, -2.47) * mm, v(3.91, -5.9) * mm, v(5.56, -7.5) * mm, v(6.88, -7.82) * mm], "startDerivative": vector(-9.88, 6.37) * mm, "endDerivative": vector(10.12, -1.27) * mm});
            skFitSpline(sketch, "E131", {"points": [v(9.18, -0.4) * mm, v(7.43, -0.16) * mm, v(5.96, -0.4) * mm, v(5.29, -0.95) * mm, v(4.62, -2.47) * mm, v(4.66, -5.55) * mm, v(6.88, -7.82) * mm], "startDerivative": vector(-10.92, 2.1) * mm, "endDerivative": vector(12.76, -9.22) * mm});
            skArc(sketch, "E132", {"start": v(-11.07, 0.24) * mm, "mid": v(-10.91, 0.5) * mm, "end": v(-10.74, 0.74) * mm});
            skArc(sketch, "E133", {"start": v(-1.03, -3.62) * mm, "mid": v(-0.98, -3.33) * mm, "end": v(-0.94, -3.03) * mm});
            skArc(sketch, "E134", {"start": v(-1.03, -1.36) * mm, "mid": v(-1.1, -1.07) * mm, "end": v(-1.18, -0.78) * mm});
            skArc(sketch, "E135", {"start": v(-3.62, 2.23) * mm, "mid": v(-3.88, 2.38) * mm, "end": v(-4.15, 2.5) * mm});
            skArc(sketch, "E136", {"start": v(-11.06, -5.2) * mm, "mid": v(-11.2, -4.94) * mm, "end": v(-11.33, -4.67) * mm});
            skArc(sketch, "E137", {"start": v(-11.76, -1.9) * mm, "mid": v(-11.73, -1.61) * mm, "end": v(-11.67, -1.32) * mm});
            skArc(sketch, "E138", {"start": v(-5.21, -7.79) * mm, "mid": v(-5.5, -7.84) * mm, "end": v(-5.8, -7.88) * mm});
            skArc(sketch, "E139", {"start": v(-9.54, -6.88) * mm, "mid": v(-9.78, -6.7) * mm, "end": v(-10, -6.5) * mm});
            skArc(sketch, "E140.trimOffspring", {"start": v(-6.82, -1.57) * mm, "mid": v(-7.07, -1.75) * mm, "end": v(-7.26, -2) * mm});
            skArc(sketch, "E141.trimOffspring", {"start": v(-5.45, -2) * mm, "mid": v(-5.63, -1.75) * mm, "end": v(-5.88, -1.57) * mm});
            skArc(sketch, "E142.trimOffspring", {"start": v(-5.88, -3.37) * mm, "mid": v(-5.63, -3.2) * mm, "end": v(-5.45, -2.94) * mm});
            skCircle(sketch, "E143", {"center": v(-6.35, -2.47) * mm, "radius": 4.14 * mm});
            skPoint(sketch, "E144.orphan", {"position": v(24.07, 9.93) * mm});
            skLineSegment(sketch, "E145", {"start": v(20.9, 3.68) * mm, "end": v(20.9, 3.69) * mm});
            skLineSegment(sketch, "E146", {"start": v(20.96, 3.2) * mm, "end": v(21.17, 3.5) * mm});
            skSolve(sketch);
        }
        {
            var Q0;
            Q0 = qSketchRegion(id + "F0", true);
            var Q1;
            Q1=makeQuery(id+"F0.imprint","IMPRINT",FACE,{"disambiguationData":[TD([[makeQuery(id+"F0.imprint","IMPRINT",EDGE,{"derivedFrom":sQuery(id+"F0.wireOp",EDGE,"E15")}),1.0]])]});
            extrude(context, id + "F1", {"entities" : qUnion([Q0, Q1]), "depth" : 25.4 * mm, "offsetDistance" : 25.4 * mm});
        }
    });
